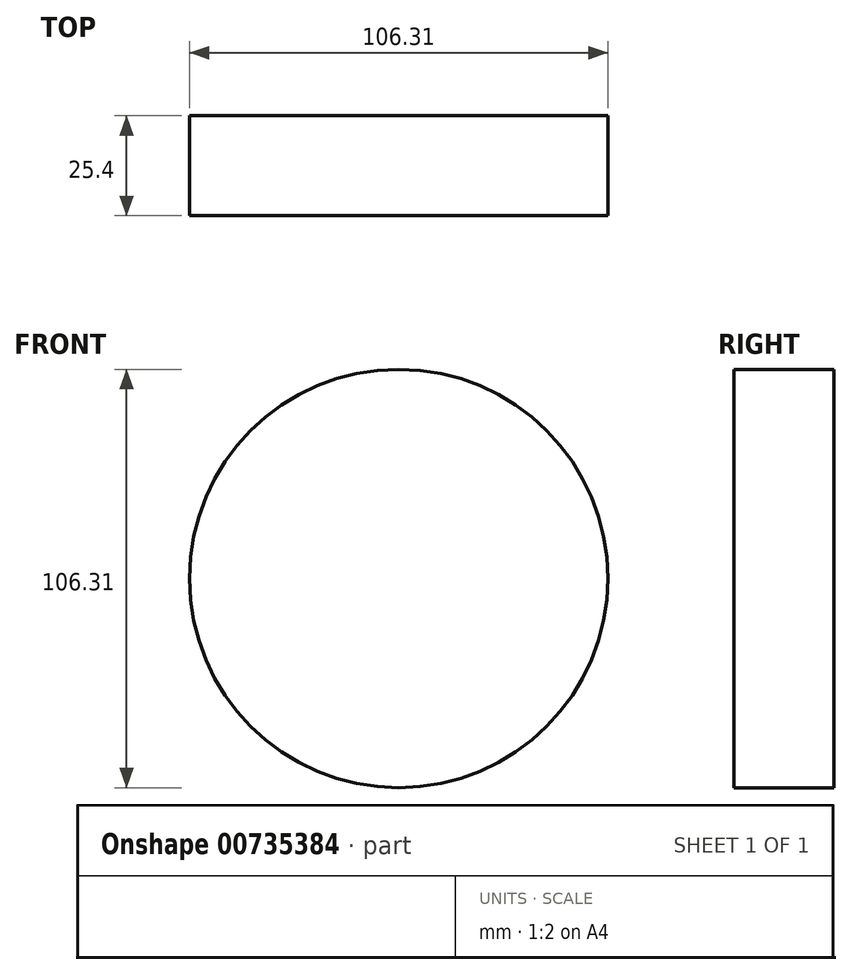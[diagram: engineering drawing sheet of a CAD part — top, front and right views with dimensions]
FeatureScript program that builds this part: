
annotation { "Feature Type Name" : "Feature", "Feature Type Description" : "" }
export const myFeature = defineFeature(function(context is Context, id is Id, definition is map)
    precondition{}
    {
        {
            var Q0;
            Q0=qCreatedBy(makeId("Front.planeOp"),FACE);
            var sketch = newSketch(context, id + "F0", { "sketchPlane" : qUnion([Q0])});
            skCircle(sketch, "E0", {"center": v(-31.75, 23.6) * mm, "radius": 53.15 * mm});
            skLineSegment(sketch, "E1", {"start": v(-62.91, 47.56) * mm, "end": v(-40.82, 55.7) * mm});
            skLineSegment(sketch, "E2", {"start": v(-62.91, 47.56) * mm, "end": v(-60.59, 9.42) * mm});
            skLineSegment(sketch, "E3", {"start": v(-59.9, 9.19) * mm, "end": v(-34.77, -5.23) * mm});
            skLineSegment(sketch, "E4", {"start": v(-34.77, -5.23) * mm, "end": v(-2.98, 6.48) * mm});
            skLineSegment(sketch, "E5", {"start": v(-2.98, 6.48) * mm, "end": v(-2.98, 47.56) * mm});
            skLineSegment(sketch, "E6", {"start": v(-2.98, 47.56) * mm, "end": v(-40.82, 55.7) * mm});
            skLineSegment(sketch, "E7", {"start": v(-52.64, 5.02) * mm, "end": v(-46.34, 16) * mm});
            skLineSegment(sketch, "E8", {"start": v(-46.34, 16) * mm, "end": v(-27.84, 17.13) * mm});
            skLineSegment(sketch, "E9", {"start": v(-27.84, 17.13) * mm, "end": v(-14.9, 2.09) * mm});
            skSolve(sketch);
        }
        {
            var Q0;
            {var subQ0=sQuery(id+"F0.wireOp",EDGE,"E7");Q0=makeQuery(id+"F0.imprint","IMPRINT",FACE,{"disambiguationData":[TD([[makeQuery(id+"F0.imprint","IMPRINT",EDGE,{"derivedFrom":subQ0}),-1.0]])]});}
            var Q1;
            Q1=makeQuery(id+"F0.imprint","IMPRINT",FACE,{"disambiguationData":[TD([[makeQuery(id+"F0.imprint","IMPRINT",EDGE,{"derivedFrom":sQuery(id+"F0.wireOp",EDGE,"E0")}),1.0]])]});
            extrude(context, id + "F1", {"entities" : qUnion([Q0, Q1]), "depth" : 25.4 * mm, "offsetDistance" : 25.4 * mm});
        }
    });
